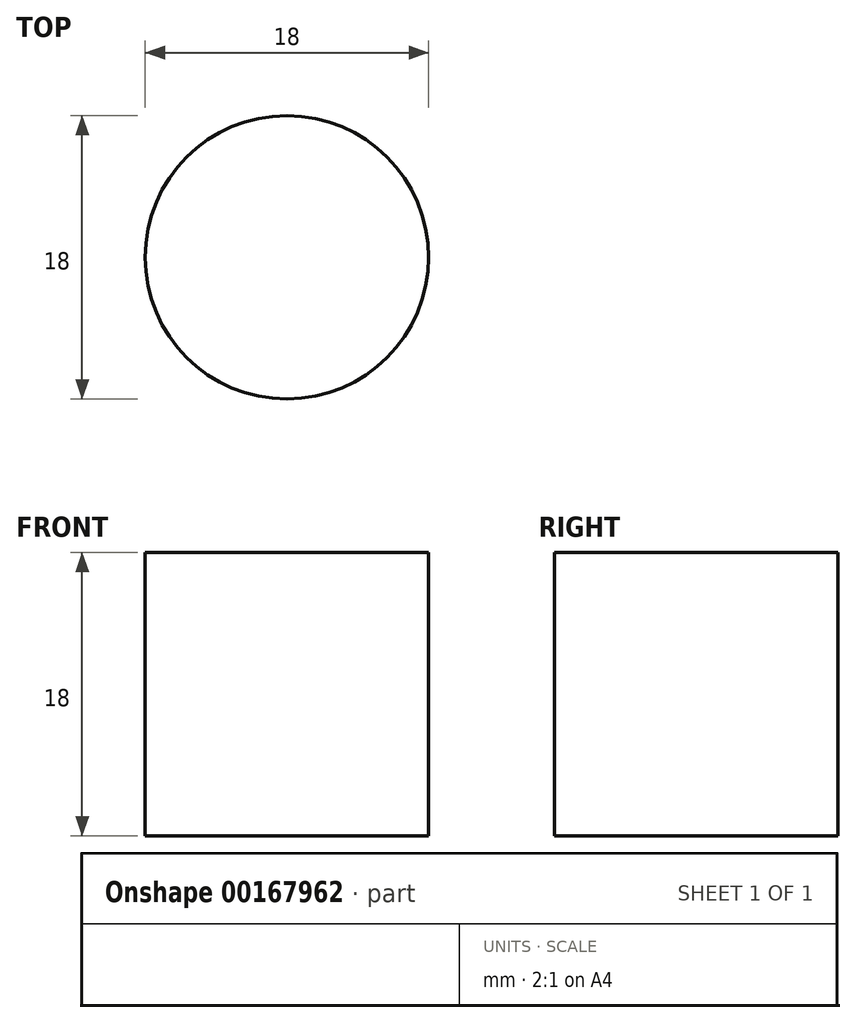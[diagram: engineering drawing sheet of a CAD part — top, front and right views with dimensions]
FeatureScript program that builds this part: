
annotation { "Feature Type Name" : "Feature", "Feature Type Description" : "" }
export const myFeature = defineFeature(function(context is Context, id is Id, definition is map)
    precondition{}
    {
        {
            var Q0;
            Q0=qCreatedBy(makeId("Top.planeOp"),FACE);
            var sketch = newSketch(context, id + "F0", { "sketchPlane" : qUnion([Q0])});
            skCircle(sketch, "E0", {"center": v(0, 0) * mm, "radius": 9 * mm});
            skSolve(sketch);
        }
        {
            var Q0;
            Q0 = qSketchRegion(id + "F0", true);
            extrude(context, id + "F1", {"entities" : qUnion([Q0]), "depth" : 18 * mm});
        }
    });
